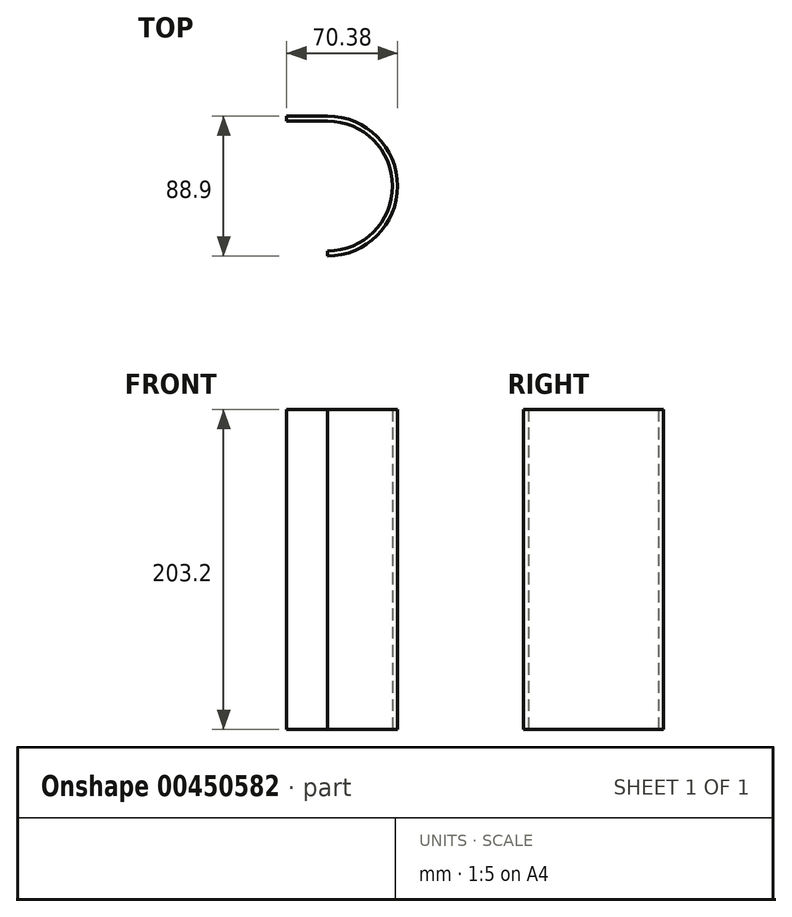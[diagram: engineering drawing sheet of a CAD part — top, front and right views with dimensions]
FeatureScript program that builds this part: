
annotation { "Feature Type Name" : "Feature", "Feature Type Description" : "" }
export const myFeature = defineFeature(function(context is Context, id is Id, definition is map)
    precondition{}
    {
        {
            var Q0;
            Q0=qCreatedBy(makeId("Top.planeOp"),FACE);
            var sketch = newSketch(context, id + "F0", { "sketchPlane" : qUnion([Q0])});
            skPoint(sketch, "E0.orphan", {"position": v(-0.17, 102.08) * mm});
            skLineSegment(sketch, "E1.MirrorCS", {"start": v(93.74, 15.35) * mm, "end": v(67.81, 15.35) * mm});
            skArc(sketch, "E2.MirrorCS", {"start": v(93.74, 12.18) * mm, "mid": v(135.02, -29.1) * mm, "end": v(93.74, -70.37) * mm});
            skArc(sketch, "E3.MirrorCS", {"start": v(93.74, 9) * mm, "mid": v(131.84, -29.1) * mm, "end": v(93.74, -67.2) * mm});
            skLineSegment(sketch, "E4.MirrorCS", {"start": v(67.81, 12.18) * mm, "end": v(93.74, 12.18) * mm});
            skLineSegment(sketch, "E5.MirrorCS", {"start": v(93.74, -70.37) * mm, "end": v(93.74, -73.55) * mm});
            skLineSegment(sketch, "E6.MirrorCS", {"start": v(67.81, 15.35) * mm, "end": v(67.81, 12.18) * mm});
            skLineSegment(sketch, "E7", {"start": v(67.81, 15.35) * mm, "end": v(93.74, 15.35) * mm});
            skArc(sketch, "E8", {"start": v(93.74, -70.37) * mm, "mid": v(135.02, -29.1) * mm, "end": v(93.74, 12.18) * mm});
            skArc(sketch, "E9.0", {"start": v(93.74, -73.55) * mm, "mid": v(138.2, -29.1) * mm, "end": v(93.74, 15.35) * mm});
            skLineSegment(sketch, "E10", {"start": v(93.74, -67.2) * mm, "end": v(93.74, -70.37) * mm});
            skSolve(sketch);
        }
        {
            var Q0;
            Q0=qSketchRegion(id+"F0",true);
            extrude(context, id + "F1", {"entities" : qUnion([Q0]), "depth" : 203.2 * mm});
        }
    });
